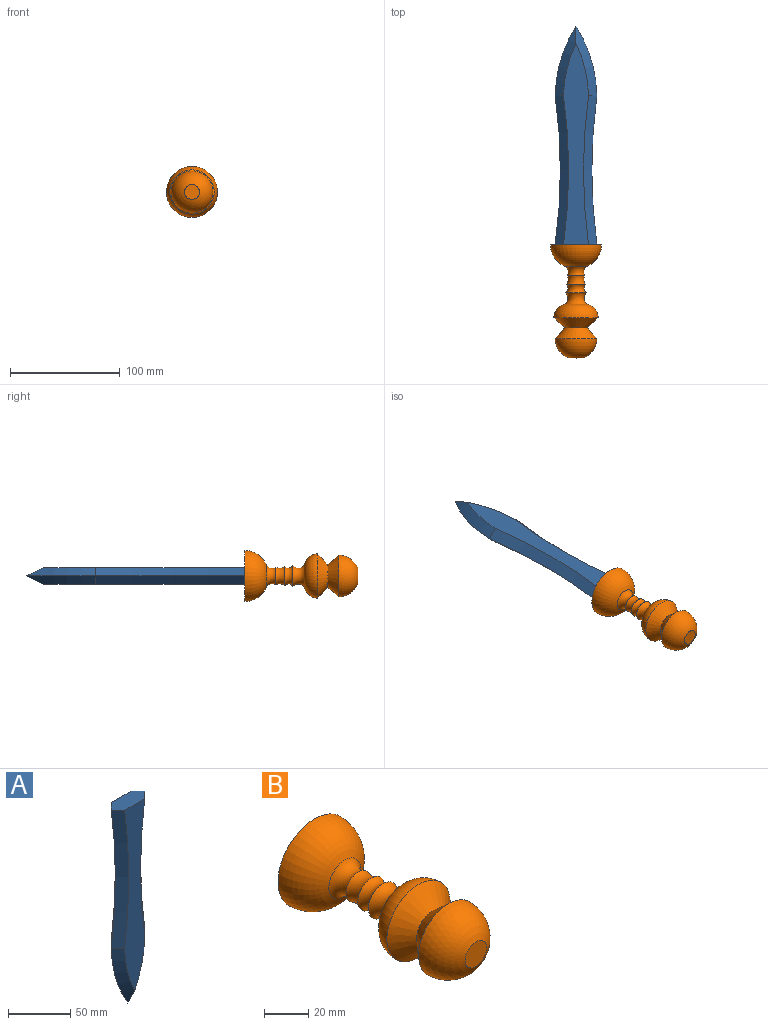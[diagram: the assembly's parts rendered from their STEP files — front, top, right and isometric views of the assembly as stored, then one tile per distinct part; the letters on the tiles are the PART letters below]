
ASSEMBLY  parts=2 mates=1
PART A: 11 faces, bbox 38.1x15.2x200.6 mm
  f0: plane 183.65x22.83mm, normal (0,1,0), area 2959.6mm2, adj f2,f6,f7,f9,f10
  f1: plane 183.65x22.83mm, normal (0,-1,0), area 2959.6mm2, adj f2,f3,f4,f5,f8
  f2: plane 38.11x15.25mm, normal (0,0,1), area 463.4mm2, adj f0,f1,f3,f4,f6,f7
  f3: cone r=486.88mm half-angle=45deg, axis (0,-1,0), area 1472.7mm2, adj f1,f2,f5,f6
  f4: cone r=499.67mm half-angle=45deg, axis (0,-1,0), area 1472.4mm2, adj f1,f2,f7,f8
  f5: cone r=118.5mm half-angle=45deg, axis (0,1,0), area 627.6mm2, adj f1,f3,f8,f9
  f6: cone r=494.5mm half-angle=45deg, axis (0,1,0), area 1472.7mm2, adj f0,f2,f3,f9
  f7: cone r=507.29mm half-angle=45deg, axis (0,1,0), area 1472.4mm2, adj f0,f2,f4,f10
  f8: cone r=118.5mm half-angle=45deg, axis (0,1,0), area 627.7mm2, adj f1,f4,f5,f10
  f9: cone r=126.12mm half-angle=45deg, axis (0,-1,0), area 627.6mm2, adj f0,f5,f6,f10
  f10: cone r=126.12mm half-angle=45deg, axis (0,-1,0), area 627.7mm2, adj f0,f7,f8,f9
PART B: 11 faces, bbox 46.5x103x46.5 mm
  f0: cone r=19.05mm half-angle=41.6deg, axis (0,-1,0), area 1235.3mm2, adj f1,f10
  f1: cone r=10.09mm half-angle=48.4deg, axis (0,1,0), area 1283.4mm2, adj f0,f2
  f2: torus R=7.48mm, axis (0,-1,0), area 1806.3mm2, adj f1,f3
  f3: torus R=14.41mm, axis (0,-1,0), area 595.8mm2, adj f2,f4
  f4: torus R=12.27mm, axis (0,-1,0), area 409.1mm2, adj f3,f5
  f5: torus R=15.86mm, axis (0,-1,0), area 410.4mm2, adj f4,f6
  f6: torus R=13.25mm, axis (0,-1,0), area 487.2mm2, adj f5,f7
  f7: torus R=2.27mm, axis (0,-1,0), area 2904.5mm2, adj f6,f8
  f8: plane 46.46x46.46mm, normal (0,1,0), area 1695.2mm2, adj f7
  f9: plane 13.68x13.68mm, normal (0,-1,0), area 146.9mm2, adj f10
  f10: sphere r=19.05mm, area 2097.3mm2, adj f0,f9
PLACE A rot(axis=(0,-0.71,0.71),180deg) t=(26.47,285.22,29.25)mm
PLACE B t=(26.47,-18.56,29.16)mm
MATE fastened A.f2 <-> B.f0  axis (0,-1,0) through (26.47,85.71,29.16)mm
